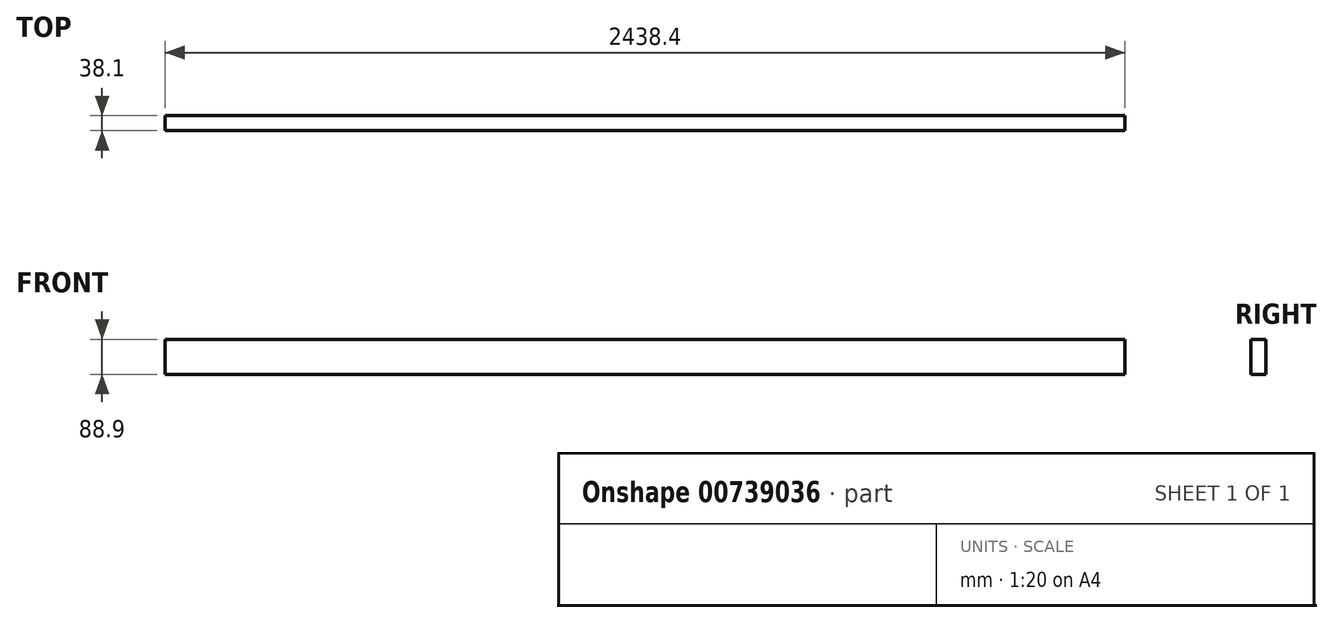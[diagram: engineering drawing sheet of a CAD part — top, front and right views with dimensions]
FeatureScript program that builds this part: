
annotation { "Feature Type Name" : "Feature", "Feature Type Description" : "" }
export const myFeature = defineFeature(function(context is Context, id is Id, definition is map)
    precondition{}
    {
        {
            var Q0;
            Q0=qCreatedBy(makeId("Front.planeOp"),FACE);
            var sketch = newSketch(context, id + "F0", { "sketchPlane" : qUnion([Q0])});
            skLineSegment(sketch, "E0.bottom", {"start": v(0, 0) * mm, "end": v(2438.4, 0) * mm});
            skLineSegment(sketch, "E0.top", {"start": v(0, 88.9) * mm, "end": v(2438.4, 88.9) * mm});
            skLineSegment(sketch, "E0.left", {"start": v(0, 0) * mm, "end": v(0, 88.9) * mm});
            skLineSegment(sketch, "E0.right", {"start": v(2438.4, 0) * mm, "end": v(2438.4, 88.9) * mm});
            skSolve(sketch);
        }
        {
            var Q0;
            Q0 = qSketchRegion(id + "F0", true);
            extrude(context, id + "F1", {"entities" : qUnion([Q0]), "depth" : 38.1 * mm, "offsetDistance" : 25.4 * mm});
        }
    });
